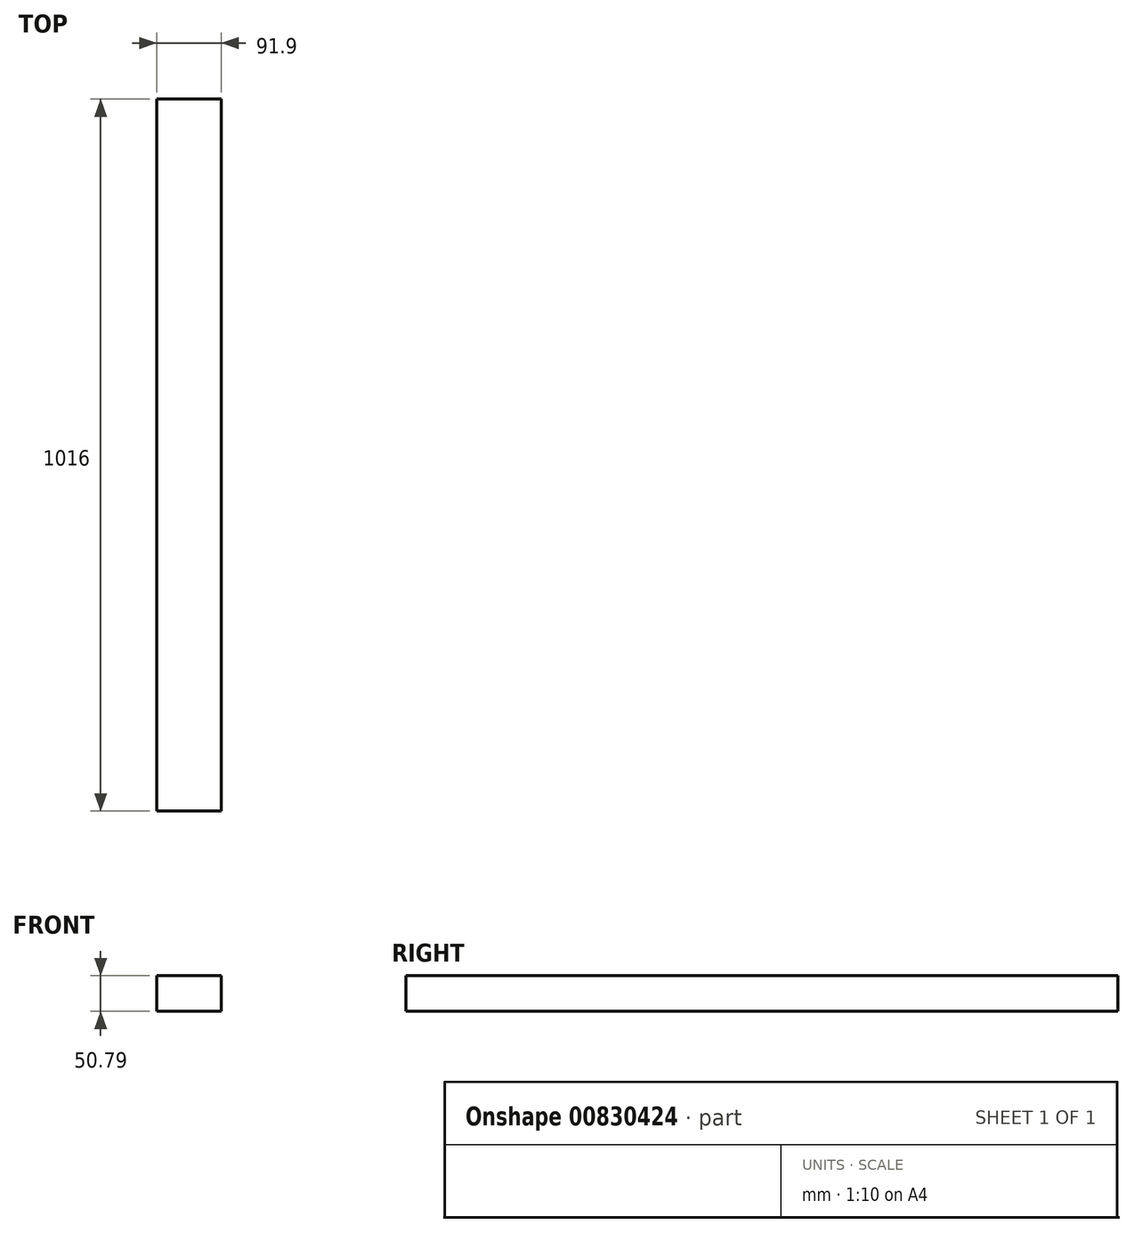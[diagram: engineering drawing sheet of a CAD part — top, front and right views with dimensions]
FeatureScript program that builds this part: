
annotation { "Feature Type Name" : "Feature", "Feature Type Description" : "" }
export const myFeature = defineFeature(function(context is Context, id is Id, definition is map)
    precondition{}
    {
        {
            var Q0;
            Q0=qCreatedBy(makeId("Front.planeOp"),FACE);
            var sketch = newSketch(context, id + "F0", { "sketchPlane" : qUnion([Q0])});
            skLineSegment(sketch, "E0.bottom", {"start": v(0, 0) * mm, "end": v(91.9, 0) * mm});
            skLineSegment(sketch, "E0.top", {"start": v(0, 50.79) * mm, "end": v(91.9, 50.79) * mm});
            skLineSegment(sketch, "E0.left", {"start": v(0, 0) * mm, "end": v(0, 50.79) * mm});
            skLineSegment(sketch, "E0.right", {"start": v(91.9, 0) * mm, "end": v(91.9, 50.79) * mm});
            skSolve(sketch);
        }
        {
            var Q0;
            Q0=makeQuery(id+"F0.imprint","IMPRINT",FACE,{"disambiguationData":[TD([[makeQuery(id+"F0.imprint","IMPRINT",EDGE,{"derivedFrom":sQuery(id+"F0.wireOp",EDGE,"E0.bottom")}),1.0]])]});
            extrude(context, id + "F1", {"entities" : qUnion([Q0]), "depth" : 1016 * mm, "offsetDistance" : 25.4 * mm});
        }
    });
